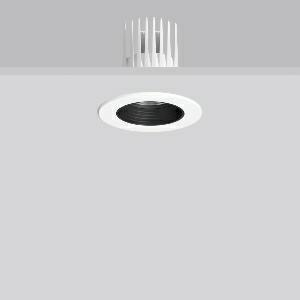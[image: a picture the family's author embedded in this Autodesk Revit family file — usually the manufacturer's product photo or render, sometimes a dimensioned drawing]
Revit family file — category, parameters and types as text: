
# Revit family: heledon_mini_e_901747_002_76_2eec
name_source: partatom
category: Lighting Fixtures
units: mm (PartAtom-declared; Revit-internal decimal feet)

## family parameters
Cut with Voids When Loaded = No
Host = Face
Light Source = No
Part Type = Normal
Room Calculation Point = No
Round Connector Dimension = Use Diameter
Shared = No

## types (1)
- HELEDON mini E (1 x LED Modul 930, 1950 lm, 3000)
    Apparent Load = 20 VA
    Approval mark = CE
    CIE Flux Codes = 95 100 100 100 100
    Color Rendering = 90
    Color Temperature = 3000
    Default Elevation = 1800 mm
    Description = Series: HELEDON mini
Round recessed downlight. Housing: die-cast aluminium, powder-coated. Black plastic ring and recessed LED to prevent glare from the side. Optical assembly with lens made of plastic (polycarbonate) for the best homogeneous light distribution - can be changed without tools. Best colour rendering index Ra>90. Suitable for Recessed ceiling mounting. Installation without tools thanks to spring fastening system. Including separate LED converter with connecting cable 600 mm.High quality converter without flickering and stroboscopic effect. Through-wiring box (5 pole) available as accessory. The following accessories can be mounted without use of tools: interchangeable lenses, decorative glasses, honeycomb louvre, clear and frosted diffusers, white interchangeable plastic ring. 
Colour: traffic white, matt (RAL 9016)
Diameter: 124 mm
Height: 3 mm
Cut-out diameter: 114 mm
Recess height: 170 mm
Luminaire: recess height: 120 mm
Lamp: LED
Socket: without socket
Colour temperature: 3000K
Colour rendering index (CRI): 92
System power: 20 W
Rated luminous flux: 1950 lm
Luminous efficiency: 98 lm/W
Control gear: Converter, dimmable, DALI
Protection class: II
Type of protection: IP 20
    Height = 0 mm  [stored 0 ft]
    Lamp = 1 x LED Modul 930
    Lamp Light Flux = 1950 lm
    Lamp count = 1
    Length = 124 mm  [stored 0.406824 ft]
    Lifetime = 50000 h
    Luminous efficacy = 98 lm/W
    Manufacturer = RZB
    ModVariant = No
    Model = 901747.002.76
    Mounting Place = Ceiling
    Mounting Type = Recessed
    Number of Poles = 1
    OnlyDefault = Yes
    Power Factor = 1
    Product Name = HELEDON mini E
    Product group = Recessed downlights
    ProductGroupID = 402
    Protection Class = Protection class II
    Protection Degree = IP 20
    RLX_Detail_Level = 1
    RLX_Emergency_Light_Flux = 0 lm
    RLX_Emergency_Type = 0
    RLX_Emergency_Type_DB = No
    RlxData = <blob elided: 136433 chars, md5=296ab787>
    Socket = socket
    Standby Power = 0 W
    System Light Flux = 1950 lm
    System Power = 20 W
    Type Comments = Product without accessories
    Type Image = 901656.002.jpg
    URL = http://relux.com
    VarID = ---
    Voltage = 230 V
    Voltage Range = 220-240 V
    Weight = 0.00 kg
    Width = 0 mm  [stored 0 ft]

note: [stored X ft] marks values corroborated as IEEE doubles in the binary element streams (Revit-internal decimal feet)

## geometry (parser evidence)
native form markers: Blend x4, Sweep x9
no freeform markers — native parametric forms only
